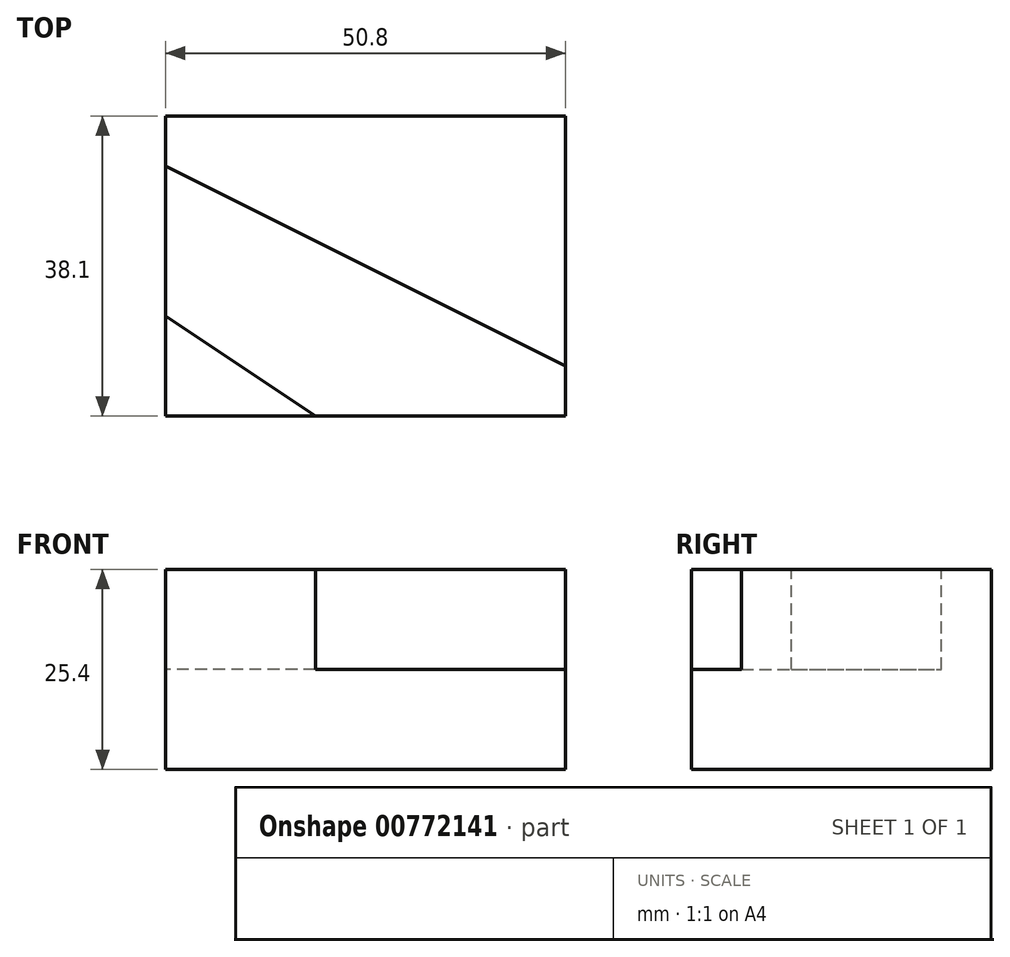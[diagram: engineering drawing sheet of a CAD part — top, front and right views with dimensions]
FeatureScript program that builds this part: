
annotation { "Feature Type Name" : "Feature", "Feature Type Description" : "" }
export const myFeature = defineFeature(function(context is Context, id is Id, definition is map)
    precondition{}
    {
        {
            var Q0;
            Q0=qCreatedBy(makeId("Front.planeOp"),FACE);
            var sketch = newSketch(context, id + "F0", { "sketchPlane" : qUnion([Q0])});
            skLineSegment(sketch, "E0", {"start": v(0, 0) * mm, "end": v(50.8, 0) * mm});
            skLineSegment(sketch, "E1", {"start": v(50.8, 0) * mm, "end": v(50.8, 25.4) * mm});
            skLineSegment(sketch, "E2", {"start": v(50.8, 25.4) * mm, "end": v(0, 25.4) * mm});
            skLineSegment(sketch, "E3", {"start": v(0, 25.4) * mm, "end": v(0, 0) * mm});
            skSolve(sketch);
        }
        {
            var Q0;
            Q0 = qSketchRegion(id + "F0", true);
            extrude(context, id + "F1", {"entities" : qUnion([Q0]), "depth" : 38.1 * mm, "offsetDistance" : 25.4 * mm});
        }
        {
            var Q0;
            Q0=makeQuery(id+"F1.opExtrude","SWEPT_FACE",FACE,{"disambiguationData":[OSD([sQuery(id+"F0.wireOp",EDGE,"E2")])]});
            var sketch = newSketch(context, id + "F2", { "sketchPlane" : qUnion([Q0])});
            skLineSegment(sketch, "E4", {"start": v(0, 0) * mm, "end": v(0, -6.35) * mm});
            skLineSegment(sketch, "E5", {"start": v(0, 0) * mm, "end": v(31.75, 0) * mm});
            skLineSegment(sketch, "E6", {"start": v(0, -38.1) * mm, "end": v(0, -25.4) * mm});
            skLineSegment(sketch, "E7", {"start": v(0, -38.1) * mm, "end": v(19.05, -38.1) * mm});
            skLineSegment(sketch, "E8", {"start": v(19.05, -38.1) * mm, "end": v(0, -25.4) * mm});
            skLineSegment(sketch, "E9", {"start": v(50.8, 0) * mm, "end": v(50.8, -31.75) * mm});
            skLineSegment(sketch, "E10", {"start": v(50.8, -31.75) * mm, "end": v(0, -6.35) * mm});
            skSolve(sketch);
        }
        {
            var Q0;
            {var subQ3=sQuery(id+"F2.wireOp",EDGE,"E8");Q0=makeQuery(id+"F2.imprint","IMPRINT",FACE,{"disambiguationData":[TD([[makeQuery(id+"F2.imprint","IMPRINT",EDGE,{"derivedFrom":subQ3}),-1.0]])]});}
            extrude(context, id + "F3", {"entities" : qUnion([Q0]), "operationType" : NewBodyOperationType.REMOVE, "oppositeDirection" : true, "depth" : 12.7 * mm, "offsetDistance" : 25.4 * mm});
        }
    });
